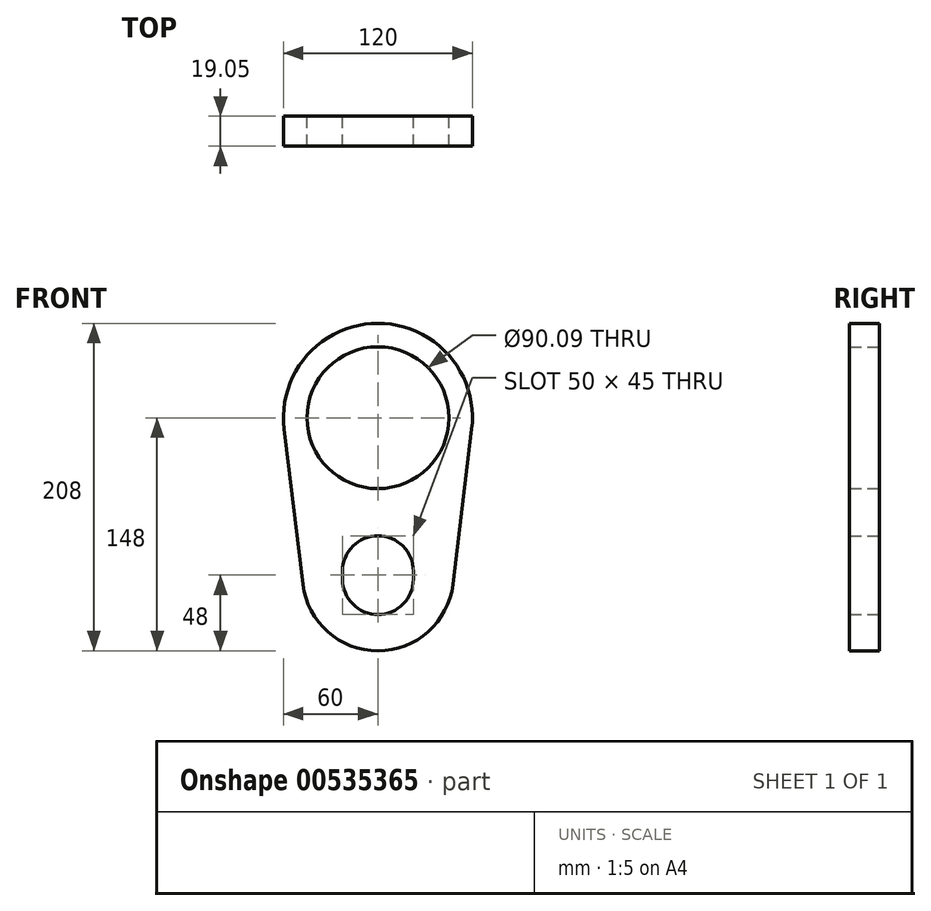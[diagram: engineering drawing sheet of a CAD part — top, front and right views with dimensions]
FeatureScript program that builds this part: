
annotation { "Feature Type Name" : "Feature", "Feature Type Description" : "" }
export const myFeature = defineFeature(function(context is Context, id is Id, definition is map)
    precondition{}
    {
        {
            var Q0;
            Q0=qCreatedBy(makeId("Front.planeOp"),FACE);
            var sketch = newSketch(context, id + "F0", { "sketchPlane" : qUnion([Q0])});
            skArc(sketch, "E0", {"start": v(59.57, -7.2) * mm, "mid": v(0, 60) * mm, "end": v(-59.57, -7.2) * mm});
            skLineSegment(sketch, "E1", {"start": v(-59.57, -7.2) * mm, "end": v(-47.65, -105.76) * mm});
            skLineSegment(sketch, "E2", {"start": v(0, 0) * mm, "end": v(0, -100) * mm, "construction": true});
            skLineSegment(sketch, "E3.MirrorCS", {"start": v(59.57, -7.2) * mm, "end": v(47.65, -105.76) * mm});
            skArc(sketch, "E4.trimOffspring", {"start": v(-47.65, -105.76) * mm, "mid": v(0, -148) * mm, "end": v(47.65, -105.76) * mm});
            skCircle(sketch, "E5", {"center": v(0, 0) * mm, "radius": 45.05 * mm});
            skLineSegment(sketch, "E6", {"start": v(0, -97.5) * mm, "end": v(0, -102.5) * mm});
            skArc(sketch, "E7.0.startCap", {"start": v(-22.5, -97.5) * mm, "mid": v(0, -75) * mm, "end": v(22.5, -97.5) * mm});
            skArc(sketch, "E7.0.endCap", {"start": v(22.5, -102.5) * mm, "mid": v(0, -125) * mm, "end": v(-22.5, -102.5) * mm});
            skLineSegment(sketch, "E7.0.left", {"start": v(22.5, -97.5) * mm, "end": v(22.5, -102.5) * mm});
            skLineSegment(sketch, "E7.0.right", {"start": v(-22.5, -97.5) * mm, "end": v(-22.5, -102.5) * mm});
            skSolve(sketch);
        }
        {
            var Q0;
            Q0=qSketchRegion(id+"F0",true);
            extrude(context, id + "F1", {"entities" : qUnion([Q0]), "depth" : 19.05 * mm, "offsetDistance" : 25.4 * mm});
        }
    });
